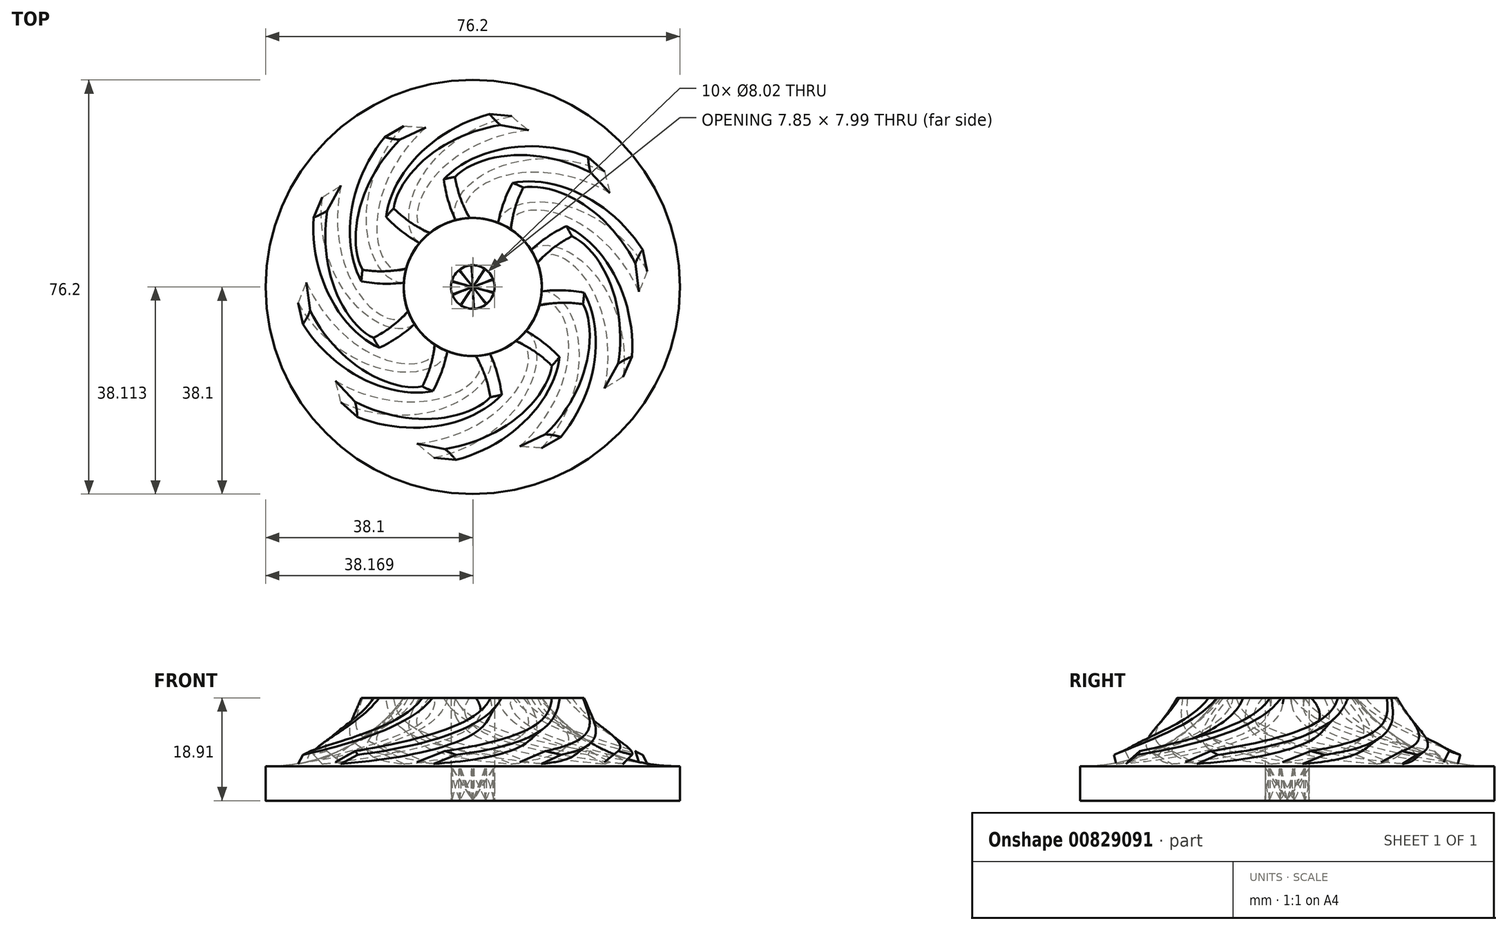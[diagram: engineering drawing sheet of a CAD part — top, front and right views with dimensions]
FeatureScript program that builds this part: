
annotation { "Feature Type Name" : "Feature", "Feature Type Description" : "" }
export const myFeature = defineFeature(function(context is Context, id is Id, definition is map)
    precondition{}
    {
        {
            var Q0;
            Q0=qCreatedBy(makeId("Front.planeOp"),FACE);
            var sketch = newSketch(context, id + "F0", { "sketchPlane" : qUnion([Q0])});
            skLineSegment(sketch, "E0", {"start": v(0, 0) * mm, "end": v(-38.1, 0) * mm});
            skLineSegment(sketch, "E1", {"start": v(-38.1, 0) * mm, "end": v(-38.1, 6.35) * mm});
            skArc(sketch, "E2", {"start": v(-38.1, 6.35) * mm, "mid": v(-23.85, 9.5) * mm, "end": v(-12.7, 18.91) * mm});
            skLineSegment(sketch, "E3", {"start": v(-12.7, 18.91) * mm, "end": v(0, 18.91) * mm});
            skLineSegment(sketch, "E4", {"start": v(0, 18.91) * mm, "end": v(0, 0) * mm});
            skSolve(sketch);
        }
        {
            var Q0;
            Q0=makeQuery(id+"F0.imprint","IMPRINT",FACE,{"disambiguationData":[TD([[makeQuery(id+"F0.imprint","IMPRINT",EDGE,{"derivedFrom":sQuery(id+"F0.wireOp",EDGE,"E0")}),-1.0]])]});
            var Q1;
            Q1=sQuery(id+"F0.wireOp",EDGE,"E4");
            revolve(context, id + "F1", {"surfaceOperationType" : NewSurfaceOperationType.NEW, "entities" : qUnion([Q0]), "axis" : qUnion([Q1]), "revolveType" : RevolveType.FULL});
        }
        {
            var Q0;
            Q0=makeQuery(id+"F1.opRevolve","SWEPT_FACE",FACE,{"disambiguationData":[OSD([sQuery(id+"F0.wireOp",EDGE,"E0")])]});
            var sketch = newSketch(context, id + "F2", { "sketchPlane" : qUnion([Q0])});
            skArc(sketch, "E5", {"start": v(0, 0) * mm, "mid": v(-18.03, 11.2) * mm, "end": v(-37.91, 3.79) * mm});
            skLineSegment(sketch, "E6", {"start": v(0, 0) * mm, "end": v(0, 5.98) * mm});
            skArc(sketch, "E7", {"start": v(0, 5.98) * mm, "mid": v(-17.37, 16.83) * mm, "end": v(-36.73, 10.14) * mm});
            skArc(sketch, "E8", {"start": v(-36.73, 10.14) * mm, "mid": v(-37.45, 6.99) * mm, "end": v(-37.91, 3.79) * mm});
            skSolve(sketch);
        }
        {
            var Q0;
            Q0=makeQuery(id+"F2.imprint","IMPRINT",FACE,{"disambiguationData":[TD([[makeQuery(id+"F2.imprint","IMPRINT",EDGE,{"derivedFrom":sQuery(id+"F2.wireOp",EDGE,"E5")}),-1.0]])]});
            var sketch = newSketch(context, id + "F3", { "sketchPlane" : qUnion([Q0])});
            skCircle(sketch, "E9", {"center": v(0, 0) * mm, "radius": 4 * mm});
            skSolve(sketch);
        }
        {
            var Q0;
            Q0 = qSketchRegion(id + "F3", true);
            extrude(context, id + "F4", {"entities" : qUnion([Q0]), "operationType" : NewBodyOperationType.REMOVE, "oppositeDirection" : true, "depth" : 25.4 * mm, "offsetDistance" : 25.4 * mm});
        }
        {
            var Q0;
            Q0=makeQuery(id+"F1.opRevolve","SWEPT_FACE",FACE,{"disambiguationData":[OSD([sQuery(id+"F0.wireOp",EDGE,"E3")])]});
            var sketch = newSketch(context, id + "F5", { "sketchPlane" : qUnion([Q0])});
            skArc(sketch, "E10", {"start": v(-1.96, -41.02) * mm, "mid": v(5.48, -24.46) * mm, "end": v(0, -7.15) * mm});
            skLineSegment(sketch, "E11", {"start": v(0, -7.15) * mm, "end": v(-4.19, -7.15) * mm});
            skArc(sketch, "E12", {"start": v(-4.19, -39.7) * mm, "mid": v(3.49, -23.43) * mm, "end": v(-4.19, -7.15) * mm});
            skArc(sketch, "E13", {"start": v(-1.96, -41.02) * mm, "mid": v(-2.91, -40.08) * mm, "end": v(-4.19, -39.7) * mm});
            skSolve(sketch);
        }
        {
            var Q1;
            {var subQ0=sQuery(id+"F5.wireOp",EDGE,"E13");Q1=makeQuery(id+"F5.imprint","IMPRINT",FACE,{"disambiguationData":[TD([[makeQuery(id+"F5.imprint","IMPRINT",EDGE,{"derivedFrom":subQ0}),-1.0]])]});}
            var Q2;
            Q2=makeQuery(id+"F2.imprint","IMPRINT",FACE,{"disambiguationData":[TD([[makeQuery(id+"F2.imprint","IMPRINT",EDGE,{"derivedFrom":sQuery(id+"F2.wireOp",EDGE,"E5")}),-1.0]])]});
            loft(context, id + "F6", {"operationType" : NewBodyOperationType.ADD, "sheetProfilesArray" : [{ "sheetProfileEntities" : qUnion([Q1]) }, { "sheetProfileEntities" : qUnion([Q2]) }]});
        }
        {
            var Q0;
            Q0=makeQuery(id+"F1.opRevolve","SWEPT_BODY",BODY,{"disambiguationData":[OSD([sQuery(id+"F0.wireOp",EDGE,"E0"),sQuery(id+"F0.wireOp",EDGE,"E1"),sQuery(id+"F0.wireOp",EDGE,"E2"),sQuery(id+"F0.wireOp",EDGE,"E3"),sQuery(id+"F0.wireOp",EDGE,"E4")])]});
            var Q1;
            Q1=makeQuery(id+"F4.boolean.opBoolean","INTERSECT",EDGE,{"derivedFrom":[makeQuery(id+"F1.opRevolve","SWEPT_FACE",FACE,{"disambiguationData":[OSD([sQuery(id+"F0.wireOp",EDGE,"E3")])]}),makeQuery(id+"F4.opExtrude","SWEPT_FACE",FACE,{"disambiguationData":[OSD([sQuery(id+"F3.wireOp",EDGE,"E9")])]})]});
            circularPattern(context, id + "F7", {"entities" : qUnion([Q0]), "axis" : qUnion([Q1]), "angle" : 360 * degree, "instanceCount" : 10, "equalSpace" : true});
        }
        {
            var Q0;
            Q0=qCreatedBy(makeId("Front.planeOp"),FACE);
            var sketch = newSketch(context, id + "F8", { "sketchPlane" : qUnion([Q0])});
            skLineSegment(sketch, "E14", {"start": v(0, 0) * mm, "end": v(-39.52, 0) * mm});
            skLineSegment(sketch, "E15", {"start": v(-39.52, 0) * mm, "end": v(-39.52, 7.44) * mm});
            skArc(sketch, "E16", {"start": v(-39.52, 7.44) * mm, "mid": v(-26.27, 11.52) * mm, "end": v(-19.14, 23.41) * mm});
            skLineSegment(sketch, "E17", {"start": v(-19.14, 23.41) * mm, "end": v(-58.8, 23.41) * mm});
            skLineSegment(sketch, "E18", {"start": v(-58.8, 23.41) * mm, "end": v(-58.8, -12.4) * mm});
            skLineSegment(sketch, "E19", {"start": v(-58.8, -12.4) * mm, "end": v(0, -12.4) * mm});
            skLineSegment(sketch, "E20", {"start": v(0, -12.4) * mm, "end": v(0, 0) * mm});
            skSolve(sketch);
        }
        {
            var Q0;
            Q0=makeQuery(id+"F8.imprint","IMPRINT",FACE,{"disambiguationData":[TD([[makeQuery(id+"F8.imprint","IMPRINT",EDGE,{"derivedFrom":sQuery(id+"F8.wireOp",EDGE,"E14")}),1.0]])]});
            var Q1;
            Q1=sQuery(id+"F8.wireOp",EDGE,"E20");
            revolve(context, id + "F9", {"operationType" : NewBodyOperationType.REMOVE, "surfaceOperationType" : NewSurfaceOperationType.NEW, "entities" : qUnion([Q0]), "axis" : qUnion([Q1]), "revolveType" : RevolveType.FULL, "oppositeDirection" : true});
        }
    });
